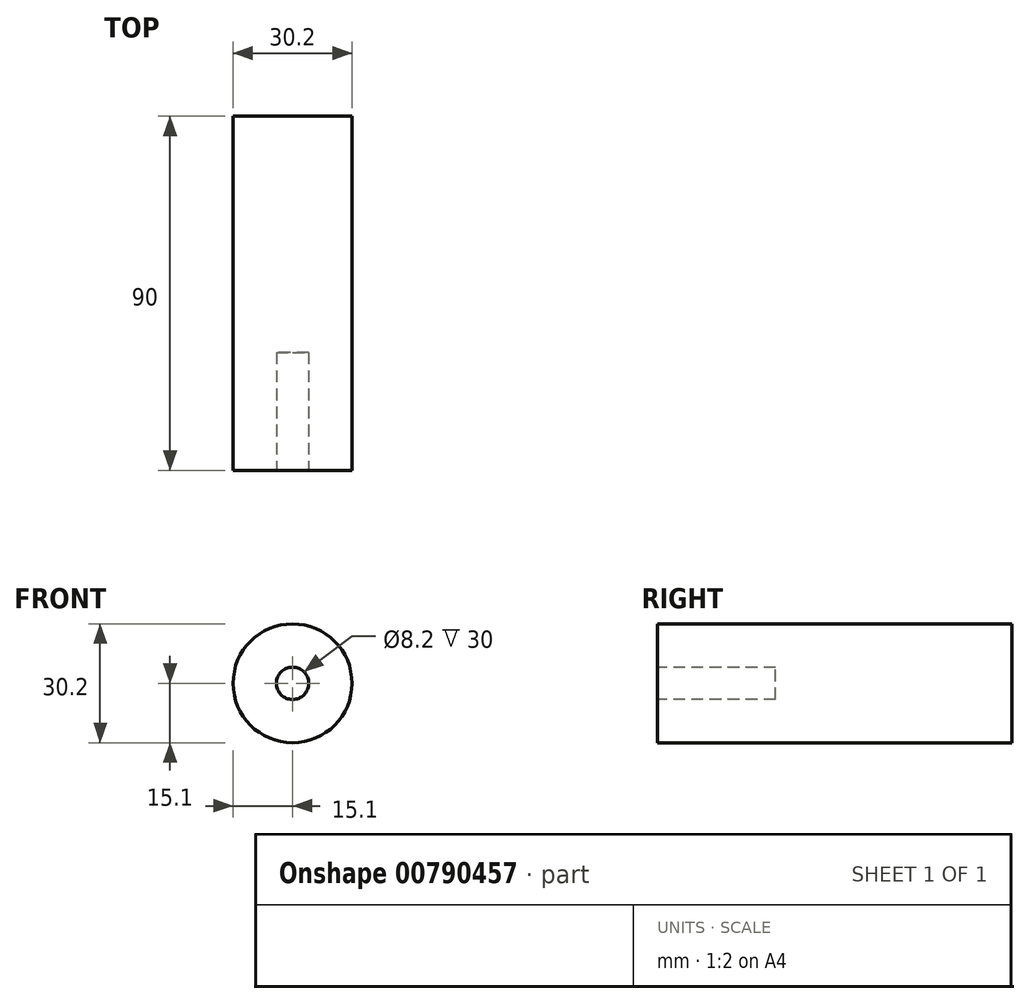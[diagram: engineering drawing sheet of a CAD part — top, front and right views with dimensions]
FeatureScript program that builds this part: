
annotation { "Feature Type Name" : "Feature", "Feature Type Description" : "" }
export const myFeature = defineFeature(function(context is Context, id is Id, definition is map)
    precondition{}
    {
        {
            var Q0;
            Q0=qCreatedBy(makeId("Top.planeOp"),FACE);
            var sketch = newSketch(context, id + "F0", { "sketchPlane" : qUnion([Q0])});
            skLineSegment(sketch, "E0.right", {"start": v(3.95, 10) * mm, "end": v(3.95, 20) * mm});
            skLineSegment(sketch, "E1.top", {"start": v(3.95, 40) * mm, "end": v(14.95, 40) * mm});
            skLineSegment(sketch, "E1.right", {"start": v(14.95, 10) * mm, "end": v(14.95, 40) * mm});
            skLineSegment(sketch, "E2", {"start": v(14.95, 10) * mm, "end": v(14.95, 114.62) * mm, "construction": true});
            skLineSegment(sketch, "E3", {"start": v(3.95, 20) * mm, "end": v(3.95, 30) * mm});
            skPoint(sketch, "E4.start.orphan", {"position": v(3, 25) * mm});
            skPoint(sketch, "E5.trimOffspring.end.orphan", {"position": v(3, 20) * mm});
            skLineSegment(sketch, "E6", {"start": v(3.95, 30) * mm, "end": v(3.95, 40) * mm});
            skLineSegment(sketch, "E7", {"start": v(14.95, 20) * mm, "end": v(3.95, 20) * mm});
            skLineSegment(sketch, "E8", {"start": v(3.95, 10) * mm, "end": v(14.95, 10) * mm});
            skLineSegment(sketch, "E9", {"start": v(-0.15, 40) * mm, "end": v(3.95, 40) * mm});
            skLineSegment(sketch, "E10", {"start": v(3.95, 30) * mm, "end": v(14.95, 30) * mm});
            skLineSegment(sketch, "E11.bottom", {"start": v(-0.15, 40) * mm, "end": v(14.95, 40) * mm});
            skLineSegment(sketch, "E11.top", {"start": v(-0.15, 100) * mm, "end": v(14.95, 100) * mm});
            skLineSegment(sketch, "E11.left", {"start": v(-0.15, 40) * mm, "end": v(-0.15, 100) * mm});
            skLineSegment(sketch, "E11.right", {"start": v(14.95, 40) * mm, "end": v(14.95, 100) * mm});
            skPoint(sketch, "E1.bottom.start.orphan", {"position": v(3.95, 0) * mm});
            skPoint(sketch, "E12.orphan", {"position": v(14.95, 0) * mm});
            skPoint(sketch, "E13.orphan", {"position": v(3.95, 25) * mm});
            skSolve(sketch);
        }
        {
            var Q0;
            {var subQ3=sQuery(id+"F0.wireOp",EDGE,"8NDevQcz-xsZ3-tm24-l13A-LveEBOFPASGn");Q0=makeQuery(id+"F0.imprint","IMPRINT",FACE,{"disambiguationData":[TD([[makeQuery(id+"F0.imprint","IMPRINT",EDGE,{"derivedFrom":subQ3}),1.0]])]});}
            var Q1;
            {var subQ0=sQuery(id+"F0.wireOp",EDGE,"8NDevQcz-xsZ3-tm24-l13A-LveEBOFPASGn");Q1=makeQuery(id+"F0.imprint","IMPRINT",FACE,{"disambiguationData":[TD([[makeQuery(id+"F0.imprint","IMPRINT",EDGE,{"derivedFrom":subQ0}),-1.0]])]});}
            var Q2;
            {var subQ3=sQuery(id+"F0.wireOp",EDGE,"vgcMQvv2-o3FH-ISmm-CDDC-TbBEyxOUiqTf");Q2=makeQuery(id+"F0.imprint","IMPRINT",FACE,{"disambiguationData":[TD([[makeQuery(id+"F0.imprint","IMPRINT",EDGE,{"derivedFrom":subQ3}),-1.0]])]});}
            var Q3;
            {var subQ0=sQuery(id+"F0.wireOp",EDGE,"vgcMQvv2-o3FH-ISmm-CDDC-TbBEyxOUiqTf");Q3=makeQuery(id+"F0.imprint","IMPRINT",FACE,{"disambiguationData":[TD([[makeQuery(id+"F0.imprint","IMPRINT",EDGE,{"derivedFrom":subQ0}),1.0]])]});}
            var Q4;
            Q4=makeQuery(id+"F0.imprint","IMPRINT",FACE,{"disambiguationData":[TD([[makeQuery(id+"F0.imprint","IMPRINT",EDGE,{"derivedFrom":sQuery(id+"F0.wireOp",EDGE,"E0.right")}),-1.0]])]});
            var Q5;
            {var subQ7=sQuery(id+"F0.wireOp",EDGE,"E7");Q5=makeQuery(id+"F0.imprint","IMPRINT",FACE,{"disambiguationData":[TD([[makeQuery(id+"F0.imprint","IMPRINT",EDGE,{"derivedFrom":subQ7}),-1.0]])]});}
            var Q6;
            {var subQ4=sQuery(id+"F0.wireOp",EDGE,"E6");Q6=makeQuery(id+"F0.imprint","IMPRINT",FACE,{"disambiguationData":[TD([[makeQuery(id+"F0.imprint","IMPRINT",EDGE,{"derivedFrom":subQ4}),-1.0]])]});}
            var Q7;
            Q7=makeQuery(id+"F0.imprint","IMPRINT",FACE,{"disambiguationData":[TD([[makeQuery(id+"F0.imprint","IMPRINT",EDGE,{"derivedFrom":sQuery(id+"F0.wireOp",EDGE,"E11.top")}),-1.0]])]});
            var Q8;
            Q8=sQuery(id+"F0.wireOp",EDGE,"E11.left");
            revolve(context, id + "F1", {"surfaceOperationType" : NewSurfaceOperationType.NEW, "entities" : qUnion([Q0, Q1, Q2, Q3, Q4, Q5, Q6, Q7]), "axis" : qUnion([Q8]), "revolveType" : RevolveType.FULL});
        }
    });
